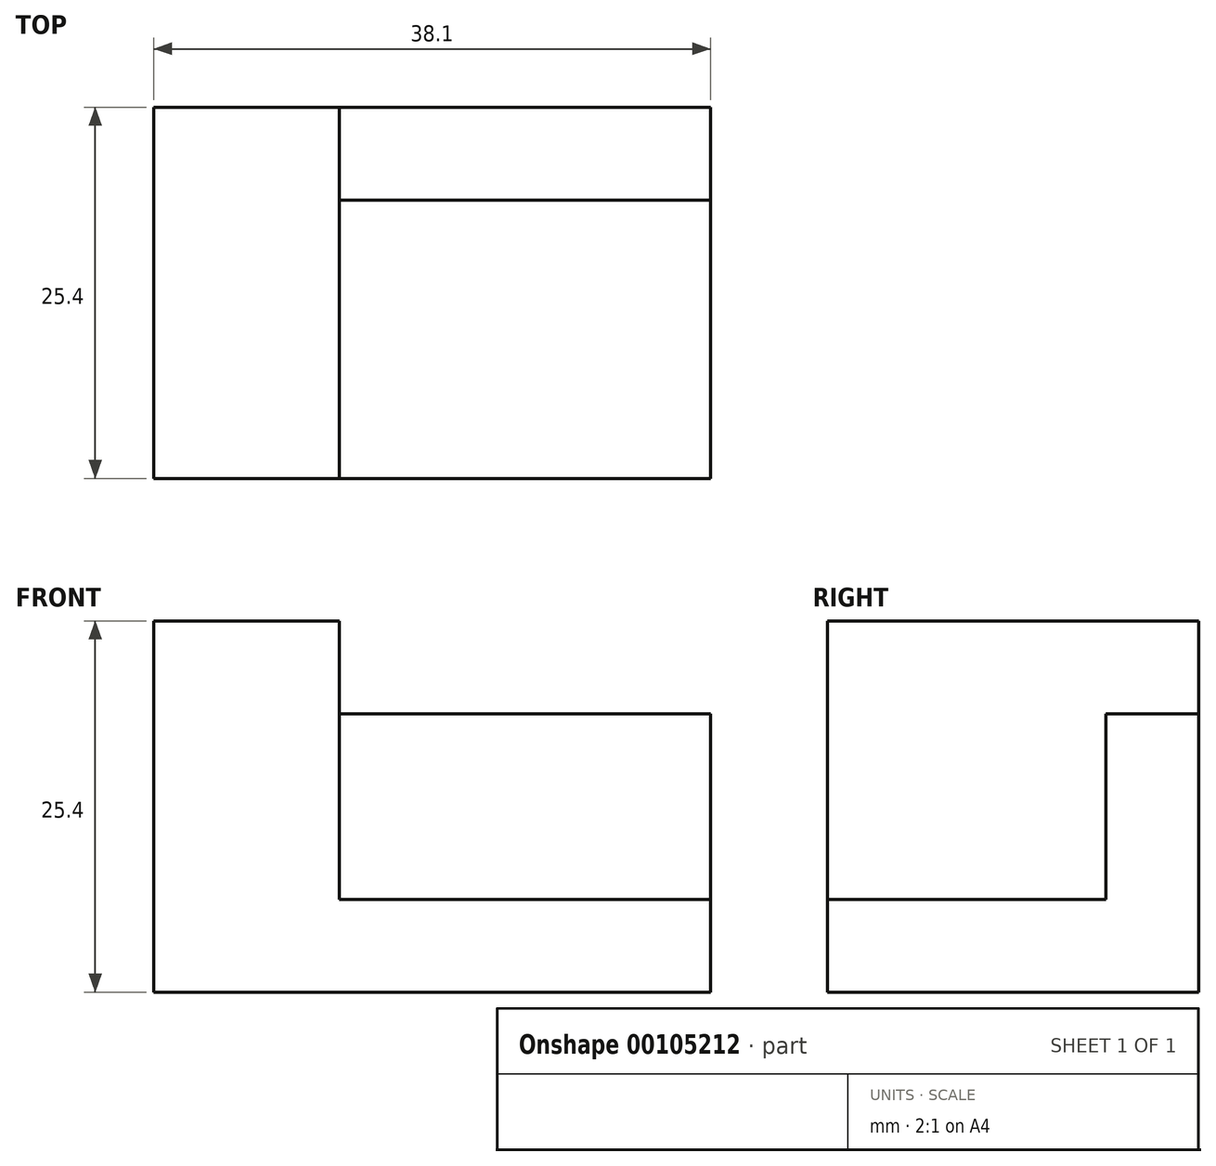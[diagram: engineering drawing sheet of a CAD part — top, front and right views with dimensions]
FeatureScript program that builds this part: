
annotation { "Feature Type Name" : "Feature", "Feature Type Description" : "" }
export const myFeature = defineFeature(function(context is Context, id is Id, definition is map)
    precondition{}
    {
        {
            var Q0;
            Q0=qCreatedBy(makeId("Front.planeOp"),FACE);
            var sketch = newSketch(context, id + "F0", { "sketchPlane" : qUnion([Q0])});
            skLineSegment(sketch, "E0", {"start": v(0, 0) * mm, "end": v(0, 25.4) * mm});
            skLineSegment(sketch, "E1", {"start": v(0, 25.4) * mm, "end": v(12.7, 25.4) * mm});
            skLineSegment(sketch, "E2", {"start": v(12.7, 25.4) * mm, "end": v(12.7, 6.35) * mm});
            skLineSegment(sketch, "E3", {"start": v(12.7, 6.35) * mm, "end": v(38.1, 6.35) * mm});
            skLineSegment(sketch, "E4", {"start": v(38.1, 6.35) * mm, "end": v(38.1, 0) * mm});
            skLineSegment(sketch, "E5", {"start": v(38.1, 0) * mm, "end": v(0, 0) * mm});
            skLineSegment(sketch, "E6", {"start": v(12.7, 19.05) * mm, "end": v(38.1, 19.05) * mm});
            skLineSegment(sketch, "E7", {"start": v(38.1, 19.05) * mm, "end": v(38.1, 6.35) * mm});
            skSolve(sketch);
        }
        {
            var Q0;
            Q0=makeQuery(id+"F0.imprint","IMPRINT",FACE,{"disambiguationData":[TD([[makeQuery(id+"F0.imprint","IMPRINT",EDGE,{"derivedFrom":sQuery(id+"F0.wireOp",EDGE,"E0")}),-1.0]])]});
            extrude(context, id + "F1", {"entities" : qUnion([Q0]), "depth" : 25.4 * mm});
        }
        {
            var Q0;
            {var subQ0=sQuery(id+"F0.wireOp",EDGE,"E3");Q0=makeQuery(id+"F0.imprint","IMPRINT",FACE,{"disambiguationData":[TD([[makeQuery(id+"F0.imprint","IMPRINT",EDGE,{"derivedFrom":subQ0}),1.0]])]});}
            extrude(context, id + "F2", {"entities" : qUnion([Q0]), "operationType" : NewBodyOperationType.ADD, "depth" : 6.35 * mm});
        }
    });
